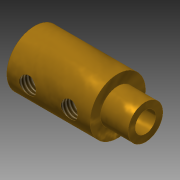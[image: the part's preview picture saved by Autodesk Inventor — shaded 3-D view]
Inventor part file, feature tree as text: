
AUTODESK INVENTOR PART (.ipt)
format: ipt  version: 2014 (Build 180170000, 170)  size: 120,320 bytes
history: native  units: mm
features: sketch x3, other x2, extrude x2, hole x1
ambient origin geometry x8: Origin, YZ Plane, XZ Plane, XY Plane, X Axis, Y Axis, Z Axis, Center Point
bodies: Body1 (feature_tree)
feature tree (8):
  other  "Твердое тело1"
  extrude  "Выдавливание1"  Depth=3.0mm
  extrude  "Выдавливание2"  Depth=8.0mm
  other  "РабПлоскость1"
  hole  "Отверстие1"  [1 undecoded]
  sketch  "Эскиз1"
  sketch  "Эскиз2"
  sketch  "Эскиз3"
note: 1 required parameter value undecoded (feature->parameter linkage not recoverable at this tier; creation-order binding heuristic only, values carry confidence <= 0.55)
